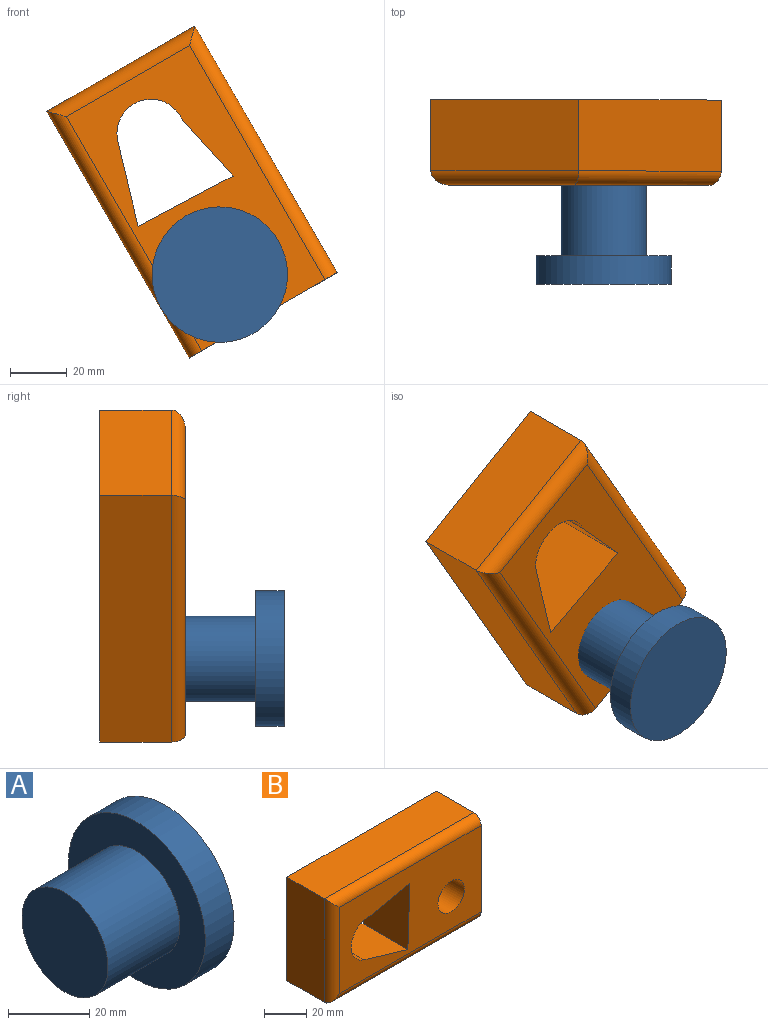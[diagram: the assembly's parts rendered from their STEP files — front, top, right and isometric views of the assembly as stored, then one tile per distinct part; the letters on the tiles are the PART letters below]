
ASSEMBLY  parts=2 mates=1
PART A: 5 faces, bbox 35x47.6x47.6 mm
  f0: cylinder r=23.78mm len=47.55mm, axis (-1,0,0), area 1494mm2, adj f1,f2
  f1: plane 47.55x47.55mm, normal (1,0,0), area 1776.1mm2, adj f0
  f2: plane 47.55x47.55mm, normal (-1,0,0), area 1073.1mm2, adj f0,f3
  f3: cylinder r=14.96mm len=29.92mm, axis (1,0,0), area 2349.8mm2, adj f2,f4
  f4: plane 29.92x29.92mm, normal (-1,0,0), area 703mm2, adj f3
PART B: 14 faces, bbox 100x30x60 mm
  f0: plane 100x25mm, normal (0,0,1), area 2500mm2, adj f1,f7,f8,f11
  f1: plane 60x25mm, normal (-1,0,0), area 1500mm2, adj f0,f2,f8,f12
  f2: plane 100x25mm, normal (0,0,-1), area 2500mm2, adj f1,f7,f8,f13
  f3: cylinder r=12mm len=30mm, axis (0,-1,0), area 1077.7mm2, adj f4,f6,f8,f9
  f4: plane 30x25.66mm, normal (0.21,0,-0.98), area 787.7mm2, adj f3,f5,f8,f9
  f5: plane 37.69x30mm, normal (-1,0,0.04), area 1131.5mm2, adj f4,f6,f8,f9
  f6: plane 30x29.37mm, normal (0.29,0,0.96), area 919.1mm2, adj f3,f5,f8,f9
  f7: plane 60x30mm, normal (1,0,0), area 1789.3mm2, adj f0,f2,f8,f9,f11,f13
  f8: plane 100x60mm, normal (0,1,0), area 4701.6mm2, adj f0,f1,f2,f3,f4,f5,f6,f7
  f9: plane 95x50mm, normal (0,-1,0), area 3451.6mm2, adj f3,f4,f5,f6,f7,f10,f11,f12
  f10: cylinder r=8.89mm len=30mm, axis (0,-1,0), area 1675.5mm2, adj f8,f9
  f11: cylinder r=5mm len=100mm, axis (-1,0,0), area 771.1mm2, adj f0,f7,f9,f12
  f12: cylinder r=5mm len=60mm, axis (0,0,-1), area 442.7mm2, adj f1,f9,f11,f13
  f13: cylinder r=5mm len=100mm, axis (1,0,0), area 771.1mm2, adj f2,f7,f9,f12
PLACE A rot(axis=(-0.69,0.69,-0.19),158.9deg) t=(-24.24,-24.7,34.45)mm
PLACE B rot(axis=(0,1,0),60deg) t=(8.95,0,-5.37)mm
MATE slider A.f0 <-> B.f10  axis (0,-1,0) through (1.97,0.3,-10.95)mm
